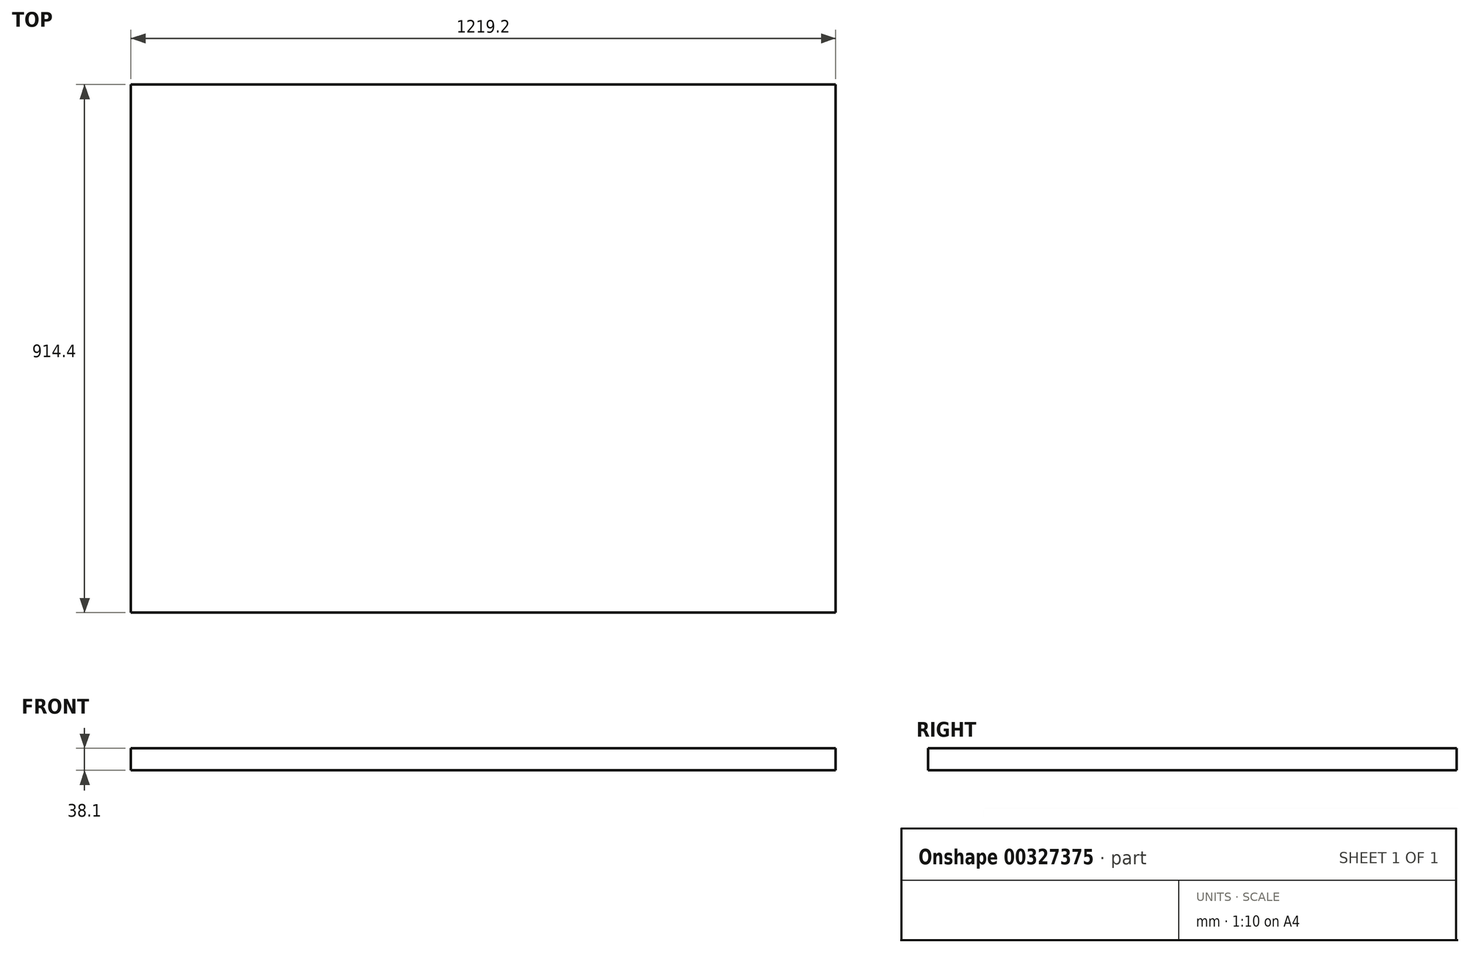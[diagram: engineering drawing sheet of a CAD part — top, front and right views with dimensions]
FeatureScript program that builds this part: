
annotation { "Feature Type Name" : "Feature", "Feature Type Description" : "" }
export const myFeature = defineFeature(function(context is Context, id is Id, definition is map)
    precondition{}
    {
        {
            var Q0;
            Q0=qCreatedBy(makeId("Top.planeOp"),FACE);
            var sketch = newSketch(context, id + "F0", { "sketchPlane" : qUnion([Q0])});
            skLineSegment(sketch, "E0.bottom", {"start": v(0, 0) * mm, "end": v(1828.8, 0) * mm});
            skLineSegment(sketch, "E0.top", {"start": v(0, -88.9) * mm, "end": v(1828.8, -88.9) * mm});
            skLineSegment(sketch, "E0.left", {"start": v(0, 0) * mm, "end": v(0, -88.9) * mm});
            skLineSegment(sketch, "E0.right", {"start": v(1828.8, 0) * mm, "end": v(1828.8, -88.9) * mm});
            skSolve(sketch);
        }
        {
            var Q0;
            Q0 = qSketchRegion(id + "F0", true);
            extrude(context, id + "F1", {"entities" : qUnion([Q0]), "depth" : 38.1 * mm});
        }
        {
            var Q0;
            Q0=makeQuery(id+"F1.opExtrude","SWEPT_BODY",BODY,{"disambiguationData":[OSD([sQuery(id+"F0.wireOp",EDGE,"E0.bottom"),sQuery(id+"F0.wireOp",EDGE,"E0.top"),sQuery(id+"F0.wireOp",EDGE,"E0.left"),sQuery(id+"F0.wireOp",EDGE,"E0.right")])]});
            deleteBodies(context, id + "F2", {"entities" : qUnion([Q0])});
        }
        {
            var Q0;
            Q0=qCreatedBy(makeId("Top.planeOp"),FACE);
            var sketch = newSketch(context, id + "F3", { "sketchPlane" : qUnion([Q0])});
            skLineSegment(sketch, "E1.bottom", {"start": v(0, 0) * mm, "end": v(1219.2, 0) * mm});
            skLineSegment(sketch, "E1.top", {"start": v(0, 914.4) * mm, "end": v(1219.2, 914.4) * mm});
            skLineSegment(sketch, "E1.left", {"start": v(0, 0) * mm, "end": v(0, 914.4) * mm});
            skLineSegment(sketch, "E1.right", {"start": v(1219.2, 0) * mm, "end": v(1219.2, 914.4) * mm});
            skSolve(sketch);
        }
        {
            var Q0;
            Q0 = qSketchRegion(id + "F3", true);
            extrude(context, id + "F4", {"entities" : qUnion([Q0]), "depth" : 38.1 * mm});
        }
    });
